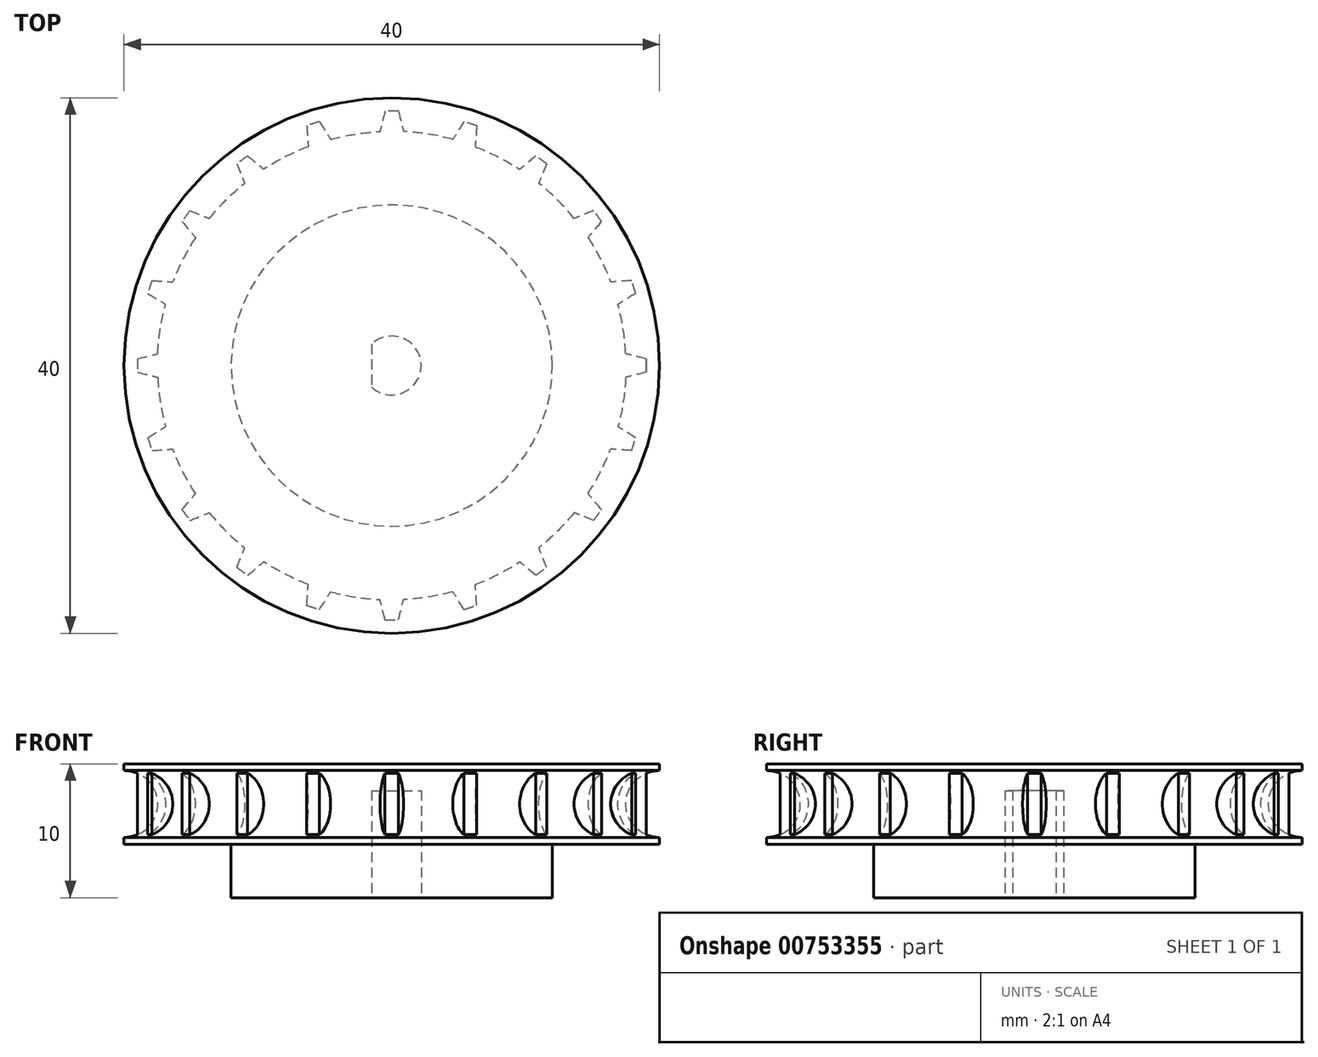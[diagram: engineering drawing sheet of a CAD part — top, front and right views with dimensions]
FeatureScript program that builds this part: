
annotation { "Feature Type Name" : "Feature", "Feature Type Description" : "" }
export const myFeature = defineFeature(function(context is Context, id is Id, definition is map)
    precondition{}
    {
        {
            var Q0;
            Q0=qCreatedBy(makeId("Right.planeOp"),FACE);
            var sketch = newSketch(context, id + "F0", { "sketchPlane" : qUnion([Q0])});
            skLineSegment(sketch, "E0", {"start": v(-12, -4) * mm, "end": v(0, -4) * mm});
            skLineSegment(sketch, "E1", {"start": v(-12, -4) * mm, "end": v(-12, 0) * mm});
            skLineSegment(sketch, "E2", {"start": v(-12, 0) * mm, "end": v(-20, 0) * mm});
            skLineSegment(sketch, "E3", {"start": v(0, 6) * mm, "end": v(-20, 6) * mm});
            skLineSegment(sketch, "E4", {"start": v(0, 6) * mm, "end": v(0, -4) * mm});
            skLineSegment(sketch, "E5", {"start": v(-20, 5.5) * mm, "end": v(-20, 6) * mm});
            skLineSegment(sketch, "E6", {"start": v(-20, 0.5) * mm, "end": v(-20, 0) * mm});
            skArc(sketch, "E7", {"start": v(-20, 0.5) * mm, "mid": v(-17.5, 3) * mm, "end": v(-20, 5.5) * mm});
            skSolve(sketch);
        }
        {
            var Q0;
            Q0=qSketchRegion(id+"F0",true);
            var Q1;
            Q1=sQuery(id+"F0.wireOp",EDGE,"E4");
            revolve(context, id + "F1", {"surfaceOperationType" : NewSurfaceOperationType.NEW, "entities" : qUnion([Q0]), "axis" : qUnion([Q1]), "revolveType" : RevolveType.FULL});
        }
        {
            var Q0;
            Q0=makeQuery(id+"F1.opRevolve","SWEPT_FACE",FACE,{"disambiguationData":[OSD([sQuery(id+"F0.wireOp",EDGE,"E0")])]});
            var sketch = newSketch(context, id + "F2", { "sketchPlane" : qUnion([Q0])});
            skCircle(sketch, "E8", {"center": v(0, 0) * mm, "radius": 2.2 * mm});
            skLineSegment(sketch, "E9", {"start": v(-1.5, -1.6) * mm, "end": v(-1.5, 1.6) * mm});
            skSolve(sketch);
        }
        {
            var Q0;
            {var subQ0=sQuery(id+"F2.wireOp",EDGE,"E9");Q0=makeQuery(id+"F2.imprint","IMPRINT",FACE,{"disambiguationData":[TD([[makeQuery(id+"F2.imprint","IMPRINT",EDGE,{"derivedFrom":subQ0}),-1.0]])]});}
            extrude(context, id + "F3", {"entities" : qUnion([Q0]), "operationType" : NewBodyOperationType.REMOVE, "oppositeDirection" : true, "depth" : 8 * mm, "offsetDistance" : 25 * mm});
        }
        {
            var Q0;
            Q0=makeQuery(id+"F1.opRevolve","SWEPT_FACE",FACE,{"disambiguationData":[OSD([sQuery(id+"F0.wireOp",EDGE,"E3")])]});
            var sketch = newSketch(context, id + "F4", { "sketchPlane" : qUnion([Q0])});
            skLineSegment(sketch, "E10", {"start": v(-17, 1) * mm, "end": v(-17, 0) * mm});
            skLineSegment(sketch, "E11", {"start": v(-17, 0) * mm, "end": v(-17, -1) * mm});
            skLineSegment(sketch, "E12", {"start": v(-17, -1) * mm, "end": v(-19, -0.5) * mm});
            skLineSegment(sketch, "E13", {"start": v(-19, -0.5) * mm, "end": v(-19, 0.5) * mm});
            skLineSegment(sketch, "E14", {"start": v(-19, 0.5) * mm, "end": v(-17, 1) * mm});
            skLineSegment(sketch, "E15.1.0", {"start": v(-18.22, -5.4) * mm, "end": v(-16.48, -4.3) * mm});
            skLineSegment(sketch, "E15.1.1", {"start": v(-17.92, -6.35) * mm, "end": v(-18.22, -5.4) * mm});
            skLineSegment(sketch, "E15.1.2", {"start": v(-16.17, -5.25) * mm, "end": v(-15.86, -6.2) * mm});
            skLineSegment(sketch, "E15.1.3", {"start": v(-16.48, -4.3) * mm, "end": v(-16.17, -5.25) * mm});
            skLineSegment(sketch, "E15.1.4", {"start": v(-15.86, -6.2) * mm, "end": v(-17.92, -6.35) * mm});
            skLineSegment(sketch, "E15.2.0", {"start": v(-15.67, -10.76) * mm, "end": v(-14.34, -9.18) * mm});
            skLineSegment(sketch, "E15.2.1", {"start": v(-15.08, -11.57) * mm, "end": v(-15.67, -10.76) * mm});
            skLineSegment(sketch, "E15.2.2", {"start": v(-13.75, -10) * mm, "end": v(-13.17, -10.8) * mm});
            skLineSegment(sketch, "E15.2.3", {"start": v(-14.34, -9.18) * mm, "end": v(-13.75, -10) * mm});
            skLineSegment(sketch, "E15.2.4", {"start": v(-13.17, -10.8) * mm, "end": v(-15.08, -11.57) * mm});
            skLineSegment(sketch, "E15.3.0", {"start": v(-11.57, -15.08) * mm, "end": v(-10.8, -13.17) * mm});
            skLineSegment(sketch, "E15.3.1", {"start": v(-10.76, -15.67) * mm, "end": v(-11.57, -15.08) * mm});
            skLineSegment(sketch, "E15.3.2", {"start": v(-10, -13.75) * mm, "end": v(-9.18, -14.34) * mm});
            skLineSegment(sketch, "E15.3.3", {"start": v(-10.8, -13.17) * mm, "end": v(-10, -13.75) * mm});
            skLineSegment(sketch, "E15.3.4", {"start": v(-9.18, -14.34) * mm, "end": v(-10.76, -15.67) * mm});
            skLineSegment(sketch, "E15.4.0", {"start": v(-6.35, -17.92) * mm, "end": v(-6.2, -15.86) * mm});
            skLineSegment(sketch, "E15.4.1", {"start": v(-5.4, -18.22) * mm, "end": v(-6.35, -17.92) * mm});
            skLineSegment(sketch, "E15.4.2", {"start": v(-5.25, -16.17) * mm, "end": v(-4.3, -16.48) * mm});
            skLineSegment(sketch, "E15.4.3", {"start": v(-6.2, -15.86) * mm, "end": v(-5.25, -16.17) * mm});
            skLineSegment(sketch, "E15.4.4", {"start": v(-4.3, -16.48) * mm, "end": v(-5.4, -18.22) * mm});
            skLineSegment(sketch, "E15.5.0", {"start": v(-0.5, -19) * mm, "end": v(-1, -17) * mm});
            skLineSegment(sketch, "E15.5.1", {"start": v(0.5, -19) * mm, "end": v(-0.5, -19) * mm});
            skLineSegment(sketch, "E15.5.2", {"start": v(0, -17) * mm, "end": v(1, -17) * mm});
            skLineSegment(sketch, "E15.5.3", {"start": v(-1, -17) * mm, "end": v(0, -17) * mm});
            skLineSegment(sketch, "E15.5.4", {"start": v(1, -17) * mm, "end": v(0.5, -19) * mm});
            skLineSegment(sketch, "E15.6.0", {"start": v(5.4, -18.22) * mm, "end": v(4.3, -16.48) * mm});
            skLineSegment(sketch, "E15.6.1", {"start": v(6.35, -17.92) * mm, "end": v(5.4, -18.22) * mm});
            skLineSegment(sketch, "E15.6.2", {"start": v(5.25, -16.17) * mm, "end": v(6.2, -15.86) * mm});
            skLineSegment(sketch, "E15.6.3", {"start": v(4.3, -16.48) * mm, "end": v(5.25, -16.17) * mm});
            skLineSegment(sketch, "E15.6.4", {"start": v(6.2, -15.86) * mm, "end": v(6.35, -17.92) * mm});
            skLineSegment(sketch, "E15.7.0", {"start": v(10.76, -15.67) * mm, "end": v(9.18, -14.34) * mm});
            skLineSegment(sketch, "E15.7.1", {"start": v(11.57, -15.08) * mm, "end": v(10.76, -15.67) * mm});
            skLineSegment(sketch, "E15.7.2", {"start": v(10, -13.75) * mm, "end": v(10.8, -13.17) * mm});
            skLineSegment(sketch, "E15.7.3", {"start": v(9.18, -14.34) * mm, "end": v(10, -13.75) * mm});
            skLineSegment(sketch, "E15.7.4", {"start": v(10.8, -13.17) * mm, "end": v(11.57, -15.08) * mm});
            skLineSegment(sketch, "E15.8.0", {"start": v(15.08, -11.57) * mm, "end": v(13.17, -10.8) * mm});
            skLineSegment(sketch, "E15.8.1", {"start": v(15.67, -10.76) * mm, "end": v(15.08, -11.57) * mm});
            skLineSegment(sketch, "E15.8.2", {"start": v(13.75, -10) * mm, "end": v(14.34, -9.18) * mm});
            skLineSegment(sketch, "E15.8.3", {"start": v(13.17, -10.8) * mm, "end": v(13.75, -10) * mm});
            skLineSegment(sketch, "E15.8.4", {"start": v(14.34, -9.18) * mm, "end": v(15.67, -10.76) * mm});
            skLineSegment(sketch, "E15.9.0", {"start": v(17.92, -6.35) * mm, "end": v(15.86, -6.2) * mm});
            skLineSegment(sketch, "E15.9.1", {"start": v(18.22, -5.4) * mm, "end": v(17.92, -6.35) * mm});
            skLineSegment(sketch, "E15.9.2", {"start": v(16.17, -5.25) * mm, "end": v(16.48, -4.3) * mm});
            skLineSegment(sketch, "E15.9.3", {"start": v(15.86, -6.2) * mm, "end": v(16.17, -5.25) * mm});
            skLineSegment(sketch, "E15.9.4", {"start": v(16.48, -4.3) * mm, "end": v(18.22, -5.4) * mm});
            skLineSegment(sketch, "E15.10.0", {"start": v(19, -0.5) * mm, "end": v(17, -1) * mm});
            skLineSegment(sketch, "E15.10.1", {"start": v(19, 0.5) * mm, "end": v(19, -0.5) * mm});
            skLineSegment(sketch, "E15.10.2", {"start": v(17, 0) * mm, "end": v(17, 1) * mm});
            skLineSegment(sketch, "E15.10.3", {"start": v(17, -1) * mm, "end": v(17, 0) * mm});
            skLineSegment(sketch, "E15.10.4", {"start": v(17, 1) * mm, "end": v(19, 0.5) * mm});
            skLineSegment(sketch, "E15.11.0", {"start": v(18.22, 5.4) * mm, "end": v(16.48, 4.3) * mm});
            skLineSegment(sketch, "E15.11.1", {"start": v(17.92, 6.35) * mm, "end": v(18.22, 5.4) * mm});
            skLineSegment(sketch, "E15.11.2", {"start": v(16.17, 5.25) * mm, "end": v(15.86, 6.2) * mm});
            skLineSegment(sketch, "E15.11.3", {"start": v(16.48, 4.3) * mm, "end": v(16.17, 5.25) * mm});
            skLineSegment(sketch, "E15.11.4", {"start": v(15.86, 6.2) * mm, "end": v(17.92, 6.35) * mm});
            skLineSegment(sketch, "E15.12.0", {"start": v(15.67, 10.76) * mm, "end": v(14.34, 9.18) * mm});
            skLineSegment(sketch, "E15.12.1", {"start": v(15.08, 11.57) * mm, "end": v(15.67, 10.76) * mm});
            skLineSegment(sketch, "E15.12.2", {"start": v(13.75, 10) * mm, "end": v(13.17, 10.8) * mm});
            skLineSegment(sketch, "E15.12.3", {"start": v(14.34, 9.18) * mm, "end": v(13.75, 10) * mm});
            skLineSegment(sketch, "E15.12.4", {"start": v(13.17, 10.8) * mm, "end": v(15.08, 11.57) * mm});
            skLineSegment(sketch, "E15.13.0", {"start": v(11.57, 15.08) * mm, "end": v(10.8, 13.17) * mm});
            skLineSegment(sketch, "E15.13.1", {"start": v(10.76, 15.67) * mm, "end": v(11.57, 15.08) * mm});
            skLineSegment(sketch, "E15.13.2", {"start": v(10, 13.75) * mm, "end": v(9.18, 14.34) * mm});
            skLineSegment(sketch, "E15.13.3", {"start": v(10.8, 13.17) * mm, "end": v(10, 13.75) * mm});
            skLineSegment(sketch, "E15.13.4", {"start": v(9.18, 14.34) * mm, "end": v(10.76, 15.67) * mm});
            skLineSegment(sketch, "E15.14.0", {"start": v(6.35, 17.92) * mm, "end": v(6.2, 15.86) * mm});
            skLineSegment(sketch, "E15.14.1", {"start": v(5.4, 18.22) * mm, "end": v(6.35, 17.92) * mm});
            skLineSegment(sketch, "E15.14.2", {"start": v(5.25, 16.17) * mm, "end": v(4.3, 16.48) * mm});
            skLineSegment(sketch, "E15.14.3", {"start": v(6.2, 15.86) * mm, "end": v(5.25, 16.17) * mm});
            skLineSegment(sketch, "E15.14.4", {"start": v(4.3, 16.48) * mm, "end": v(5.4, 18.22) * mm});
            skLineSegment(sketch, "E15.15.0", {"start": v(0.5, 19) * mm, "end": v(1, 17) * mm});
            skLineSegment(sketch, "E15.15.1", {"start": v(-0.5, 19) * mm, "end": v(0.5, 19) * mm});
            skLineSegment(sketch, "E15.15.2", {"start": v(0, 17) * mm, "end": v(-1, 17) * mm});
            skLineSegment(sketch, "E15.15.3", {"start": v(1, 17) * mm, "end": v(0, 17) * mm});
            skLineSegment(sketch, "E15.15.4", {"start": v(-1, 17) * mm, "end": v(-0.5, 19) * mm});
            skLineSegment(sketch, "E15.16.0", {"start": v(-5.4, 18.22) * mm, "end": v(-4.3, 16.48) * mm});
            skLineSegment(sketch, "E15.16.1", {"start": v(-6.35, 17.92) * mm, "end": v(-5.4, 18.22) * mm});
            skLineSegment(sketch, "E15.16.2", {"start": v(-5.25, 16.17) * mm, "end": v(-6.2, 15.86) * mm});
            skLineSegment(sketch, "E15.16.3", {"start": v(-4.3, 16.48) * mm, "end": v(-5.25, 16.17) * mm});
            skLineSegment(sketch, "E15.16.4", {"start": v(-6.2, 15.86) * mm, "end": v(-6.35, 17.92) * mm});
            skLineSegment(sketch, "E15.17.0", {"start": v(-10.76, 15.67) * mm, "end": v(-9.18, 14.34) * mm});
            skLineSegment(sketch, "E15.17.1", {"start": v(-11.57, 15.08) * mm, "end": v(-10.76, 15.67) * mm});
            skLineSegment(sketch, "E15.17.2", {"start": v(-10, 13.75) * mm, "end": v(-10.8, 13.17) * mm});
            skLineSegment(sketch, "E15.17.3", {"start": v(-9.18, 14.34) * mm, "end": v(-10, 13.75) * mm});
            skLineSegment(sketch, "E15.17.4", {"start": v(-10.8, 13.17) * mm, "end": v(-11.57, 15.08) * mm});
            skLineSegment(sketch, "E15.18.0", {"start": v(-15.08, 11.57) * mm, "end": v(-13.17, 10.8) * mm});
            skLineSegment(sketch, "E15.18.1", {"start": v(-15.67, 10.76) * mm, "end": v(-15.08, 11.57) * mm});
            skLineSegment(sketch, "E15.18.2", {"start": v(-13.75, 10) * mm, "end": v(-14.34, 9.18) * mm});
            skLineSegment(sketch, "E15.18.3", {"start": v(-13.17, 10.8) * mm, "end": v(-13.75, 10) * mm});
            skLineSegment(sketch, "E15.18.4", {"start": v(-14.34, 9.18) * mm, "end": v(-15.67, 10.76) * mm});
            skLineSegment(sketch, "E15.19.0", {"start": v(-17.92, 6.35) * mm, "end": v(-15.86, 6.2) * mm});
            skLineSegment(sketch, "E15.19.1", {"start": v(-18.22, 5.4) * mm, "end": v(-17.92, 6.35) * mm});
            skLineSegment(sketch, "E15.19.2", {"start": v(-16.17, 5.25) * mm, "end": v(-16.48, 4.3) * mm});
            skLineSegment(sketch, "E15.19.3", {"start": v(-15.86, 6.2) * mm, "end": v(-16.17, 5.25) * mm});
            skLineSegment(sketch, "E15.19.4", {"start": v(-16.48, 4.3) * mm, "end": v(-18.22, 5.4) * mm});
            skPoint(sketch, "E15.center", {"position": v(0, 0) * mm});
            skSolve(sketch);
        }
        {
            var Q0;
            Q0 = qSketchRegion(id + "F4", true);
            extrude(context, id + "F5", {"entities" : qUnion([Q0]), "operationType" : NewBodyOperationType.ADD, "oppositeDirection" : true, "depth" : 6 * mm, "offsetDistance" : 25 * mm});
        }
    });
